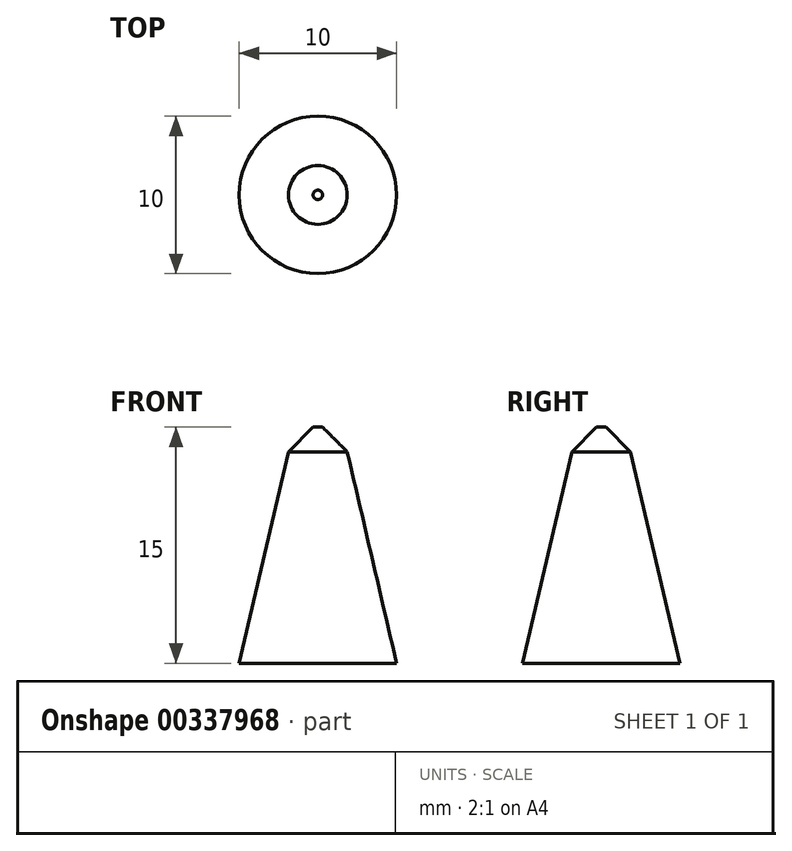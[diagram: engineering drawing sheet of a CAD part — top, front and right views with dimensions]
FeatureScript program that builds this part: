
annotation { "Feature Type Name" : "Feature", "Feature Type Description" : "" }
export const myFeature = defineFeature(function(context is Context, id is Id, definition is map)
    precondition{}
    {
        {
            var Q0;
            Q0=qCreatedBy(makeId("Top.planeOp"),FACE);
            var sketch = newSketch(context, id + "F0", { "sketchPlane" : qUnion([Q0])});
            skCircle(sketch, "E0", {"center": v(0, 0) * mm, "radius": 5 * mm});
            skSolve(sketch);
        }
        {
            var Q0;
            Q0=qCreatedBy(makeId("Top.planeOp"),FACE);
            cPlane(context, id + "F1", {"entities" : qUnion([Q0]), "cplaneType" : CPlaneType.OFFSET, "offset" : 15 * mm, "width" : 150 * mm, "height" : 150 * mm});
        }
        {
            var Q0;
            Q0=qCreatedBy(id+"F1.planeOp",FACE);
            var sketch = newSketch(context, id + "F2", { "sketchPlane" : qUnion([Q0])});
            skCircle(sketch, "E1", {"center": v(0, 0) * mm, "radius": 1.5 * mm});
            skSolve(sketch);
        }
        {
            var Q0;
            Q0=makeQuery(id+"F0.imprint","IMPRINT",FACE,{"disambiguationData":[TD([[makeQuery(id+"F0.imprint","IMPRINT",EDGE,{"derivedFrom":sQuery(id+"F0.wireOp",EDGE,"E0")}),1.0]])]});
            var Q1;
            Q1=makeQuery(id+"F2.imprint","IMPRINT",FACE,{"disambiguationData":[TD([[makeQuery(id+"F2.imprint","IMPRINT",EDGE,{"derivedFrom":sQuery(id+"F2.wireOp",EDGE,"E1")}),1.0]])]});
            loft(context, id + "F3", {"sheetProfilesArray" : [{ "sheetProfileEntities" : qUnion([Q0]) }, { "sheetProfileEntities" : qUnion([Q1]) }]});
        }
        {
            var Q0;
            Q0=makeQuery(id+"F3.opLoft","CAP_FACE",FACE,{"disambiguationData":[OSD([makeQuery(id+"F2.imprint","IMPRINT",FACE,{"disambiguationData":[TD([[makeQuery(id+"F2.imprint","IMPRINT",EDGE,{"derivedFrom":sQuery(id+"F2.wireOp",EDGE,"E1")}),1.0]])]})])],"isStart":true});
            chamfer(context, id + "F4", {"entities" : qUnion([Q0]), "chamferType" : ChamferType.OFFSET_ANGLE, "width" : 1.2 * mm, "oppositeDirection" : false, "angle" : 45 * degree, "tangentPropagation" : true});
        }
    });
